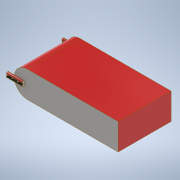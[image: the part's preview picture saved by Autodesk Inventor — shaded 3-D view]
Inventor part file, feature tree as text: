
AUTODESK INVENTOR PART (.ipt)
format: ipt  version: 2022 (Build 260153000, 153)  size: 205,824 bytes
history: native  units: mm
features: extrude x5, sketch x5
ambient origin geometry x8: Origin, YZ Plane, XZ Plane, XY Plane, X Axis, Y Axis, Z Axis, Center Point
bodies: Solid1 (feature_tree)
feature tree (10):
  extrude  "Extrusion1"  TaperAngle=0.0deg  [1 undecoded]
  extrude  "Extrusion2"  TaperAngle=0.0deg  [1 undecoded]
  extrude  "Extrusion3"  Depth=3.0mm
  extrude  "Extrusion4"  Depth=53.0mm
  extrude  "Extrusion5"  Depth=1.5mm TaperAngle=0.0deg
  sketch  "Sketch2"  dims[d0=15.0mm d1=0.0mm]
  sketch  "Sketch3"  dims[d2=51.5mm d3=0.0mm]
  sketch  "Sketch4"  dims[d4=30.0mm d5=0.0mm d6=3.0mm]
  sketch  "Sketch5"  dims[d7=6.0mm d8=53.0mm]
  sketch  "Sketch6"  dims[d9=10.5mm d10=1.5mm d11=0.0mm d12=0.75mm d13=0.75mm d14=0.0mm d15=0.0mm d16=4.5mm d17=53.0mm d18=5.25mm d19=0.0mm d20=1.5mm d21=0.0mm d22=1.5mm d23=0.75mm d24=0.75mm d25=1.5mm d26=0.0mm d27=0.0mm]
note: 2 required parameter values undecoded (feature->parameter linkage not recoverable at this tier; creation-order binding heuristic only, values carry confidence <= 0.55)
